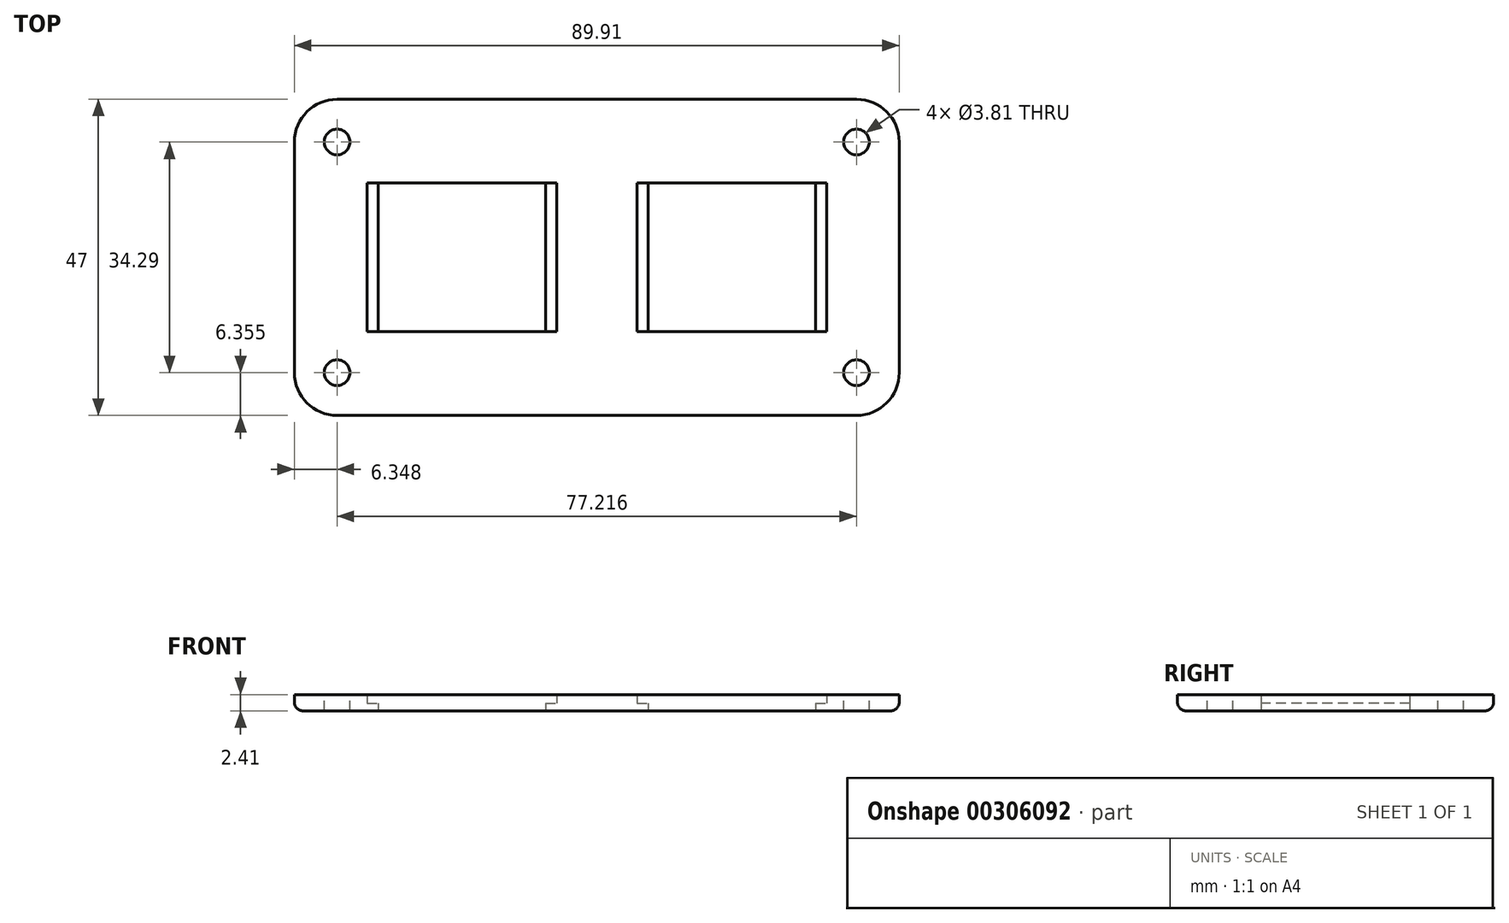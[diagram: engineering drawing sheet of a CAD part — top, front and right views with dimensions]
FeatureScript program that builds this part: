
annotation { "Feature Type Name" : "Feature", "Feature Type Description" : "" }
export const myFeature = defineFeature(function(context is Context, id is Id, definition is map)
    precondition{}
    {
        {
            var Q0;
            Q0=qCreatedBy(makeId("Top.planeOp"),FACE);
            var sketch = newSketch(context, id + "F0", { "sketchPlane" : qUnion([Q0])});
            skPoint(sketch, "E0.middle", {"position": v(0, 0) * mm});
            skLineSegment(sketch, "E1.bottom", {"start": v(-12.45, 11.05) * mm, "end": v(12.45, 11.05) * mm});
            skLineSegment(sketch, "E1.top", {"start": v(-12.45, -11.05) * mm, "end": v(12.45, -11.05) * mm});
            skLineSegment(sketch, "E1.left", {"start": v(-12.45, 11.05) * mm, "end": v(-12.45, -11.05) * mm});
            skLineSegment(sketch, "E1.right", {"start": v(12.45, 11.05) * mm, "end": v(12.45, -11.05) * mm});
            skLineSegment(sketch, "E2.bottom", {"start": v(27.69, 11.05) * mm, "end": v(52.58, 11.05) * mm});
            skLineSegment(sketch, "E2.top", {"start": v(27.69, -11.05) * mm, "end": v(52.58, -11.05) * mm});
            skLineSegment(sketch, "E2.left", {"start": v(27.69, 11.05) * mm, "end": v(27.69, -11.05) * mm});
            skLineSegment(sketch, "E2.right", {"start": v(52.58, 11.05) * mm, "end": v(52.58, -11.05) * mm});
            skLineSegment(sketch, "E3.bottom", {"start": v(-24.9, 23.5) * mm, "end": v(65.02, 23.5) * mm});
            skLineSegment(sketch, "E3.top", {"start": v(-24.9, -23.5) * mm, "end": v(65.02, -23.5) * mm});
            skLineSegment(sketch, "E3.left", {"start": v(-24.9, 23.5) * mm, "end": v(-24.9, -23.5) * mm});
            skLineSegment(sketch, "E3.right", {"start": v(65.02, 23.5) * mm, "end": v(65.02, -23.5) * mm});
            skPoint(sketch, "E4", {"position": v(-24.9, 0) * mm});
            skLineSegment(sketch, "E5", {"start": v(-12.45, 11.05) * mm, "end": v(-12.45, 23.5) * mm, "construction": true});
            skLineSegment(sketch, "E6", {"start": v(-12.45, 11.05) * mm, "end": v(-24.9, 11.05) * mm, "construction": true});
            skLineSegment(sketch, "E7", {"start": v(52.58, 11.05) * mm, "end": v(65.02, 11.05) * mm, "construction": true});
            skSolve(sketch);
        }
        {
            var Q0;
            Q0 = qSketchRegion(id + "F0", true);
            extrude(context, id + "F1", {"entities" : qUnion([Q0]), "depth" : 1.14 * mm});
        }
        {
            var Q0;
            Q0=makeQuery(id+"F1.opExtrude","CAP_FACE",FACE,{"disambiguationData":[OSD([sQuery(id+"F0.wireOp",EDGE,"E0.bottom"),sQuery(id+"F0.wireOp",EDGE,"E0.top"),sQuery(id+"F0.wireOp",EDGE,"E0.left"),sQuery(id+"F0.wireOp",EDGE,"E0.right"),sQuery(id+"F0.wireOp",EDGE,"E1.bottom"),sQuery(id+"F0.wireOp",EDGE,"E1.top"),sQuery(id+"F0.wireOp",EDGE,"E1.left"),sQuery(id+"F0.wireOp",EDGE,"E1.right")])],"isStart":false});
            var sketch = newSketch(context, id + "F2", { "sketchPlane" : qUnion([Q0])});
            skLineSegment(sketch, "E8.bottom", {"start": v(-24.9, 23.5) * mm, "end": v(65.02, 23.5) * mm});
            skLineSegment(sketch, "E8.top", {"start": v(-24.9, -23.5) * mm, "end": v(65.02, -23.5) * mm});
            skLineSegment(sketch, "E8.left", {"start": v(-24.9, 23.5) * mm, "end": v(-24.9, -23.5) * mm});
            skLineSegment(sketch, "E8.right", {"start": v(65.02, 23.5) * mm, "end": v(65.02, -23.5) * mm});
            skLineSegment(sketch, "E9.bottom", {"start": v(-14.1, 11.05) * mm, "end": v(14.1, 11.05) * mm});
            skLineSegment(sketch, "E9.top", {"start": v(-14.1, -11.05) * mm, "end": v(14.1, -11.05) * mm});
            skLineSegment(sketch, "E9.left", {"start": v(-14.1, 11.05) * mm, "end": v(-14.1, -11.05) * mm});
            skLineSegment(sketch, "E9.right", {"start": v(14.1, 11.05) * mm, "end": v(14.1, -11.05) * mm});
            skLineSegment(sketch, "E10.bottom", {"start": v(26.04, 11.05) * mm, "end": v(54.23, 11.05) * mm});
            skLineSegment(sketch, "E10.top", {"start": v(26.04, -11.05) * mm, "end": v(54.23, -11.05) * mm});
            skLineSegment(sketch, "E10.left", {"start": v(26.04, 11.05) * mm, "end": v(26.04, -11.05) * mm});
            skLineSegment(sketch, "E10.right", {"start": v(54.23, 11.05) * mm, "end": v(54.23, -11.05) * mm});
            skPoint(sketch, "E11", {"position": v(0, 11.05) * mm});
            skPoint(sketch, "E12", {"position": v(40.13, 11.05) * mm});
            skPoint(sketch, "E13", {"position": v(40.13, -11.05) * mm});
            skSolve(sketch);
        }
        {
            var Q0;
            Q0 = qSketchRegion(id + "F2", true);
            extrude(context, id + "F3", {"entities" : qUnion([Q0]), "operationType" : NewBodyOperationType.ADD, "depth" : 1.27 * mm});
        }
        {
            var Q0;
            Q0=makeQuery(id+"F3.boolean.opBoolean","MERGE",EDGE,{"derivedFrom":[makeQuery(id+"F1.opExtrude","SWEPT_EDGE",EDGE,{"disambiguationData":[OSD([sQuery(id+"F0.wireOp",EDGE,"E3.top"),sQuery(id+"F0.wireOp",EDGE,"E3.left")])]}),makeQuery(id+"F3.opExtrude","SWEPT_EDGE",EDGE,{"disambiguationData":[OSD([sQuery(id+"F2.wireOp",EDGE,"E8.top"),sQuery(id+"F2.wireOp",EDGE,"E8.left")])]})]});
            var Q1;
            Q1=makeQuery(id+"F3.boolean.opBoolean","MERGE",EDGE,{"derivedFrom":[makeQuery(id+"F1.opExtrude","SWEPT_EDGE",EDGE,{"disambiguationData":[OSD([sQuery(id+"F0.wireOp",EDGE,"E3.bottom"),sQuery(id+"F0.wireOp",EDGE,"E3.left")])]}),makeQuery(id+"F3.opExtrude","SWEPT_EDGE",EDGE,{"disambiguationData":[OSD([sQuery(id+"F2.wireOp",EDGE,"E8.bottom"),sQuery(id+"F2.wireOp",EDGE,"E8.left")])]})]});
            var Q2;
            Q2=makeQuery(id+"F3.boolean.opBoolean","MERGE",EDGE,{"derivedFrom":[makeQuery(id+"F1.opExtrude","SWEPT_EDGE",EDGE,{"disambiguationData":[OSD([sQuery(id+"F0.wireOp",EDGE,"E3.top"),sQuery(id+"F0.wireOp",EDGE,"E3.right")])]}),makeQuery(id+"F3.opExtrude","SWEPT_EDGE",EDGE,{"disambiguationData":[OSD([sQuery(id+"F2.wireOp",EDGE,"E8.top"),sQuery(id+"F2.wireOp",EDGE,"E8.right")])]})]});
            var Q3;
            Q3=makeQuery(id+"F3.boolean.opBoolean","MERGE",EDGE,{"derivedFrom":[makeQuery(id+"F1.opExtrude","SWEPT_EDGE",EDGE,{"disambiguationData":[OSD([sQuery(id+"F0.wireOp",EDGE,"E3.bottom"),sQuery(id+"F0.wireOp",EDGE,"E3.right")])]}),makeQuery(id+"F3.opExtrude","SWEPT_EDGE",EDGE,{"disambiguationData":[OSD([sQuery(id+"F2.wireOp",EDGE,"E8.bottom"),sQuery(id+"F2.wireOp",EDGE,"E8.right")])]})]});
            fillet(context, id + "F4", {"entities" : qUnion([Q0, Q1, Q2, Q3]), "radius" : 6.35 * mm, "tangentPropagation" : true, "allowEdgeOverflow" : false});
        }
        {
            var Q0;
            Q0=makeQuery(id+"F3.opExtrude","CAP_FACE",FACE,{"disambiguationData":[OSD([sQuery(id+"F2.wireOp",EDGE,"E8.bottom"),sQuery(id+"F2.wireOp",EDGE,"E8.top"),sQuery(id+"F2.wireOp",EDGE,"E8.left"),sQuery(id+"F2.wireOp",EDGE,"E8.right"),sQuery(id+"F2.wireOp",EDGE,"E9.bottom"),sQuery(id+"F2.wireOp",EDGE,"E9.top"),sQuery(id+"F2.wireOp",EDGE,"E9.left"),sQuery(id+"F2.wireOp",EDGE,"E9.right"),sQuery(id+"F2.wireOp",EDGE,"E10.bottom"),sQuery(id+"F2.wireOp",EDGE,"E10.top"),sQuery(id+"F2.wireOp",EDGE,"E10.left"),sQuery(id+"F2.wireOp",EDGE,"E10.right")])],"isStart":false});
            var sketch = newSketch(context, id + "F5", { "sketchPlane" : qUnion([Q0])});
            skCircle(sketch, "E14", {"center": v(-18.54, 17.14) * mm, "radius": 1.9 * mm});
            skCircle(sketch, "E15", {"center": v(-18.54, -17.14) * mm, "radius": 1.9 * mm});
            skCircle(sketch, "E16", {"center": v(58.67, -17.14) * mm, "radius": 1.9 * mm});
            skCircle(sketch, "E17", {"center": v(58.67, 17.14) * mm, "radius": 1.9 * mm});
            skSolve(sketch);
        }
        {
            var Q0;
            Q0 = qSketchRegion(id + "F5", true);
            var Q1;
            Q1=makeQuery(id+"F1.opExtrude","CAP_FACE",FACE,{"disambiguationData":[OSD([sQuery(id+"F0.wireOp",EDGE,"E1.bottom"),sQuery(id+"F0.wireOp",EDGE,"E1.top"),sQuery(id+"F0.wireOp",EDGE,"E1.left"),sQuery(id+"F0.wireOp",EDGE,"E1.right"),sQuery(id+"F0.wireOp",EDGE,"E2.bottom"),sQuery(id+"F0.wireOp",EDGE,"E2.top"),sQuery(id+"F0.wireOp",EDGE,"E2.left"),sQuery(id+"F0.wireOp",EDGE,"E2.right"),sQuery(id+"F0.wireOp",EDGE,"E3.bottom"),sQuery(id+"F0.wireOp",EDGE,"E3.top"),sQuery(id+"F0.wireOp",EDGE,"E3.left"),sQuery(id+"F0.wireOp",EDGE,"E3.right")])],"isStart":true});
            extrude(context, id + "F6", {"entities" : qUnion([Q0]), "operationType" : NewBodyOperationType.REMOVE, "endBound" : BoundingType.UP_TO_SURFACE, "oppositeDirection" : true, "endBoundEntityFace" : qUnion([Q1]), "depth" : 25.4 * mm});
        }
        {
            var Q0;
            {var subQ0=sQuery(id+"F0.wireOp",EDGE,"E3.left");var subQ1=sQuery(id+"F0.wireOp",EDGE,"E3.bottom");Q0=makeQuery(id+"F4.opFillet","BLEND_EDGE",EDGE,{"blendedFrom":[makeQuery(id+"F3.boolean.opBoolean","MERGE",EDGE,{"derivedFrom":[makeQuery(id+"F1.opExtrude","SWEPT_EDGE",EDGE,{"disambiguationData":[OSD([subQ1,subQ0])]}),makeQuery(id+"F3.opExtrude","SWEPT_EDGE",EDGE,{"disambiguationData":[OSD([sQuery(id+"F2.wireOp",EDGE,"E8.bottom"),sQuery(id+"F2.wireOp",EDGE,"E8.left")])]})]}),makeQuery(id+"F1.opExtrude","CAP_FACE",FACE,{"disambiguationData":[OSD([sQuery(id+"F0.wireOp",EDGE,"E1.bottom"),sQuery(id+"F0.wireOp",EDGE,"E1.top"),sQuery(id+"F0.wireOp",EDGE,"E1.left"),sQuery(id+"F0.wireOp",EDGE,"E1.right"),sQuery(id+"F0.wireOp",EDGE,"E2.bottom"),sQuery(id+"F0.wireOp",EDGE,"E2.top"),sQuery(id+"F0.wireOp",EDGE,"E2.left"),sQuery(id+"F0.wireOp",EDGE,"E2.right"),subQ1,sQuery(id+"F0.wireOp",EDGE,"E3.top"),subQ0,sQuery(id+"F0.wireOp",EDGE,"E3.right")])],"isStart":true})],"blendedInto":[makeQuery(id+"F1.opExtrude","CAP_FACE",FACE,{"disambiguationData":[OSD([sQuery(id+"F0.wireOp",EDGE,"E1.bottom"),sQuery(id+"F0.wireOp",EDGE,"E1.top"),sQuery(id+"F0.wireOp",EDGE,"E1.left"),sQuery(id+"F0.wireOp",EDGE,"E1.right"),sQuery(id+"F0.wireOp",EDGE,"E2.bottom"),sQuery(id+"F0.wireOp",EDGE,"E2.top"),sQuery(id+"F0.wireOp",EDGE,"E2.left"),sQuery(id+"F0.wireOp",EDGE,"E2.right"),subQ1,sQuery(id+"F0.wireOp",EDGE,"E3.top"),subQ0,sQuery(id+"F0.wireOp",EDGE,"E3.right")])],"isStart":true})]});}
            fillet(context, id + "F7", {"entities" : qUnion([Q0]), "radius" : 1.27 * mm, "tangentPropagation" : true, "allowEdgeOverflow" : false});
        }
    });
